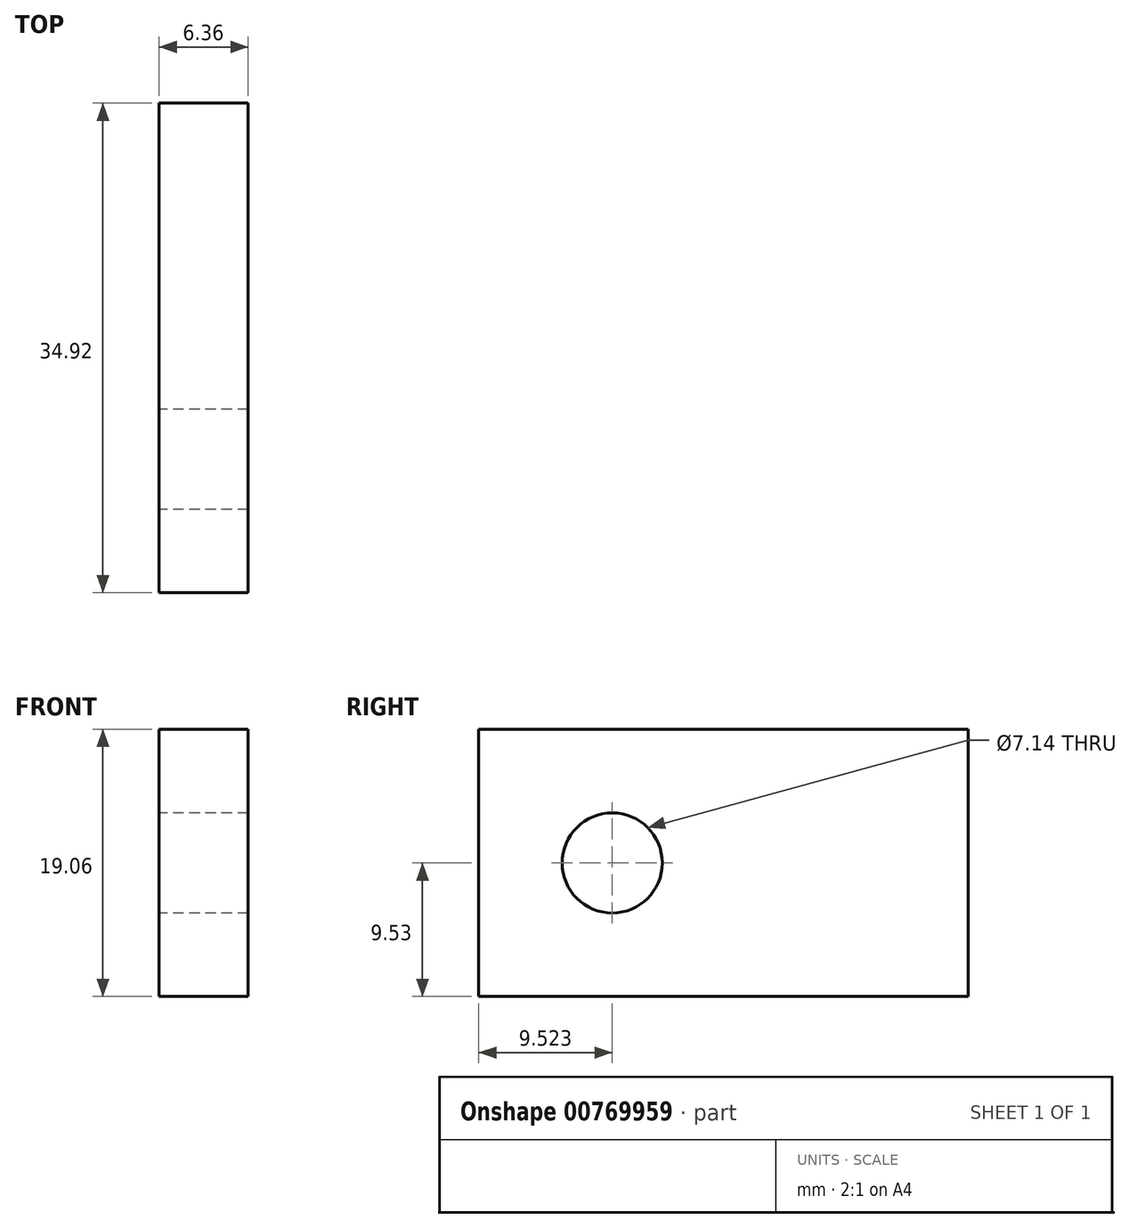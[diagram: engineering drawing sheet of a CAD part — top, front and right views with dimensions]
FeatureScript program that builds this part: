
annotation { "Feature Type Name" : "Feature", "Feature Type Description" : "" }
export const myFeature = defineFeature(function(context is Context, id is Id, definition is map)
    precondition{}
    {
        {
            var Q0;
            Q0=qCreatedBy(makeId("Right.planeOp"),FACE);
            var sketch = newSketch(context, id + "F0", { "sketchPlane" : qUnion([Q0])});
            skLineSegment(sketch, "E0.bottom", {"start": v(17.46, 9.53) * mm, "end": v(-17.46, 9.53) * mm});
            skLineSegment(sketch, "E0.top", {"start": v(17.46, -9.53) * mm, "end": v(-17.46, -9.53) * mm});
            skLineSegment(sketch, "E0.left", {"start": v(17.46, 9.53) * mm, "end": v(17.46, -9.53) * mm});
            skLineSegment(sketch, "E0.right", {"start": v(-17.46, 9.53) * mm, "end": v(-17.46, -9.53) * mm});
            skPoint(sketch, "E0.middle", {"position": v(0, 0) * mm});
            skCircle(sketch, "E1", {"center": v(-7.94, 0) * mm, "radius": 3.57 * mm});
            skSolve(sketch);
        }
        {
            var Q0;
            Q0=makeQuery(id+"F0.imprint","IMPRINT",FACE,{"disambiguationData":[TD([[makeQuery(id+"F0.imprint","IMPRINT",EDGE,{"derivedFrom":sQuery(id+"F0.wireOp",EDGE,"E0.bottom")}),1.0]])]});
            extrude(context, id + "F1", {"entities" : qUnion([Q0]), "depth" : 6.35 * mm, "offsetDistance" : 25.4 * mm, "symmetric" : true});
        }
    });
